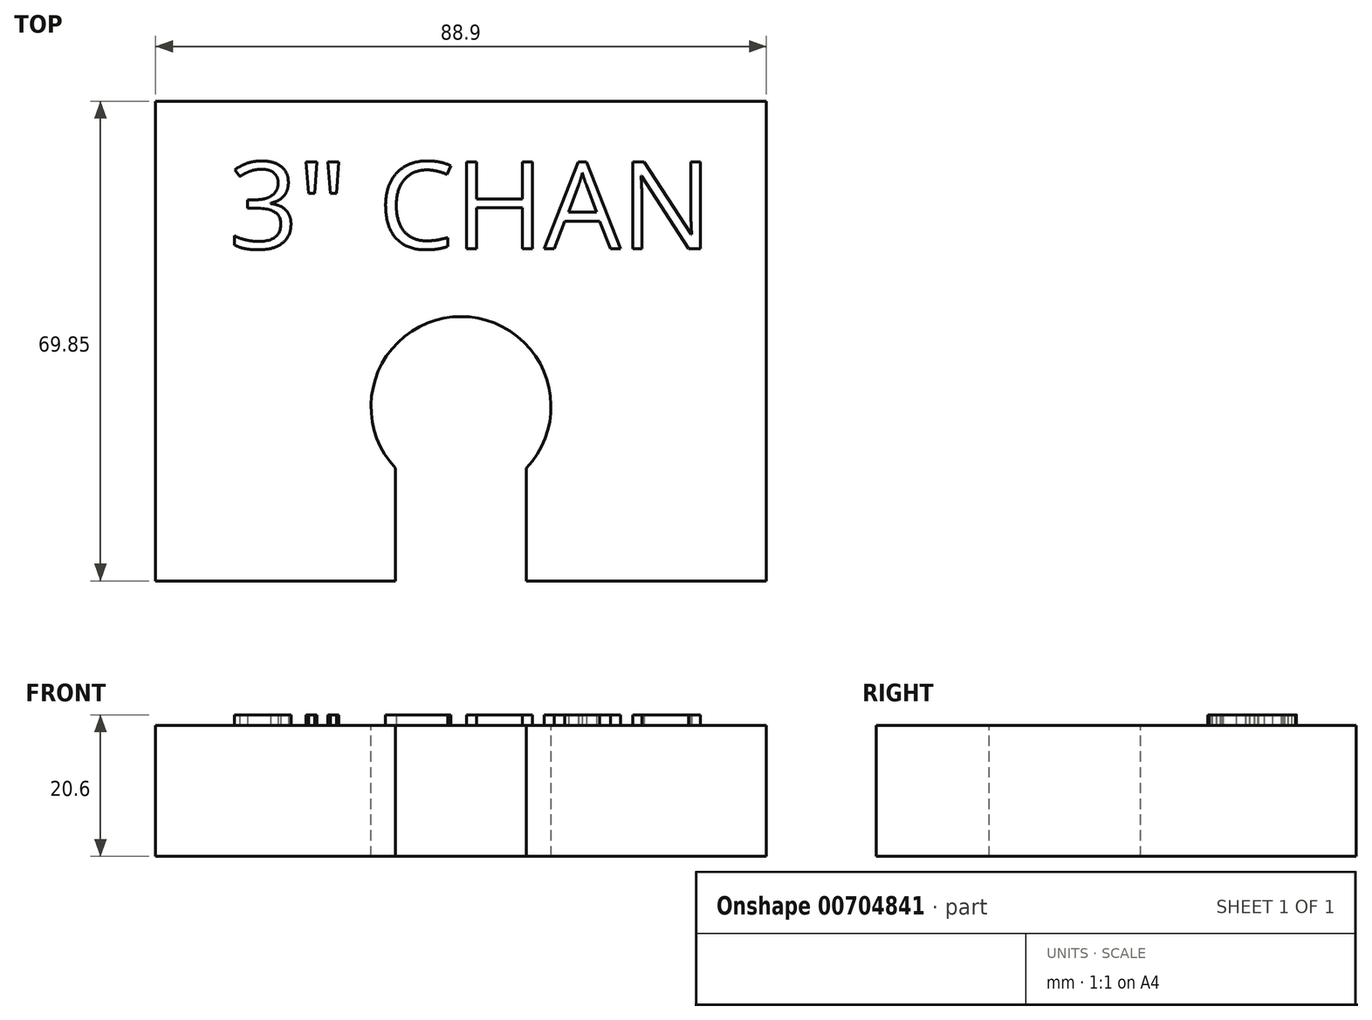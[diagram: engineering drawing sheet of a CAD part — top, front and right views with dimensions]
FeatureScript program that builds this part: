
annotation { "Feature Type Name" : "Feature", "Feature Type Description" : "" }
export const myFeature = defineFeature(function(context is Context, id is Id, definition is map)
    precondition{}
    {
        {
            var Q0;
            Q0=qCreatedBy(makeId("Top.planeOp"),FACE);
            var sketch = newSketch(context, id + "F0", { "sketchPlane" : qUnion([Q0])});
            skLineSegment(sketch, "E0.bottom", {"start": v(-53.09, 49.19) * mm, "end": v(35.81, 49.19) * mm});
            skLineSegment(sketch, "E0.top", {"start": v(-53.09, -20.66) * mm, "end": v(35.81, -20.66) * mm});
            skLineSegment(sketch, "E0.left", {"start": v(-53.09, 49.19) * mm, "end": v(-53.09, -20.66) * mm});
            skLineSegment(sketch, "E0.right", {"start": v(35.81, 49.19) * mm, "end": v(35.81, -20.66) * mm});
            skSolve(sketch);
        }
        {
            var Q0;
            Q0=makeQuery(id+"F0.imprint","IMPRINT",FACE,{"disambiguationData":[TD([[makeQuery(id+"F0.imprint","IMPRINT",EDGE,{"derivedFrom":sQuery(id+"F0.wireOp",EDGE,"E0.bottom")}),-1.0]])]});
            extrude(context, id + "F1", {"entities" : qUnion([Q0]), "depth" : 19.05 * mm, "offsetDistance" : 25.4 * mm});
        }
        {
            var Q0;
            Q0=makeQuery(id+"F1.opExtrude","CAP_FACE",FACE,{"disambiguationData":[OSD([sQuery(id+"F0.wireOp",EDGE,"E0.bottom"),sQuery(id+"F0.wireOp",EDGE,"E0.top"),sQuery(id+"F0.wireOp",EDGE,"E0.left"),sQuery(id+"F0.wireOp",EDGE,"E0.right")])],"isStart":false});
            var sketch = newSketch(context, id + "F2", { "sketchPlane" : qUnion([Q0])});
            skPoint(sketch, "E1", {"position": v(-8.64, 4.74) * mm});
            skPoint(sketch, "E1.positionSnap0", {"position": v(-8.64, -20.66) * mm});
            skArc(sketch, "E2", {"start": v(0.89, -4.25) * mm, "mid": v(-8.64, 17.84) * mm, "end": v(-18.16, -4.25) * mm});
            skLineSegment(sketch, "E3.0", {"start": v(-18.16, -4.25) * mm, "end": v(-18.16, -20.66) * mm});
            skLineSegment(sketch, "E4.0", {"start": v(0.89, -4.25) * mm, "end": v(0.89, -20.66) * mm});
            skSolve(sketch);
        }
        {
            var Q0;
            Q0=makeQuery(id+"F2.imprint","IMPRINT",FACE,{"disambiguationData":[TD([[makeQuery(id+"F2.imprint","IMPRINT",EDGE,{"derivedFrom":sQuery(id+"F2.wireOp",EDGE,"E2")}),1.0]])]});
            extrude(context, id + "F3", {"entities" : qUnion([Q0]), "operationType" : NewBodyOperationType.REMOVE, "oppositeDirection" : true, "depth" : 25.4 * mm, "offsetDistance" : 25.4 * mm});
        }
        {
            var Q0;
            Q0=makeQuery(id+"F1.opExtrude","CAP_FACE",FACE,{"disambiguationData":[OSD([sQuery(id+"F0.wireOp",EDGE,"E0.bottom"),sQuery(id+"F0.wireOp",EDGE,"E0.top"),sQuery(id+"F0.wireOp",EDGE,"E0.left"),sQuery(id+"F0.wireOp",EDGE,"E0.right")])],"isStart":false});
            var sketch = newSketch(context, id + "F4", { "sketchPlane" : qUnion([Q0])});
            skText(sketch, "E5", { "text": "3\" CHAN", "fontName": "OpenSans-Regular.ttf"});
            const initialGuessF4  = {"E5": [-0.04243, 0.02773, 1, 0, 0.0127]};
            skSetInitialGuess(sketch, initialGuessF4);
            skSolve(sketch);
        }
        {
            var Q0;
            Q0 = qSketchRegion(id + "F4", true);
            var Q1;
            Q1 = qConstructionFilter(qBodyType(qCreatedBy(id + "F4" ,EDGE), BodyType.WIRE), ConstructionObject.NO);
            extrude(context, id + "F5", {"entities" : qUnion([Q0]), "operationType" : NewBodyOperationType.ADD, "surfaceEntities" : qUnion([Q1]), "depth" : 1.55 * mm, "offsetDistance" : 25.4 * mm});
        }
    });
